# Revit family: IEK_Розетка_ОУ_C_ЗК_16А_4_мест_IP54_ГЕРМЕС_PLUS
name_source: partatom
category: Электрические приборы
units: mm (PartAtom-declared; Revit-internal decimal feet)

## family parameters
Всегда вертикально = Да
На основе рабочей плоскости = Нет
Общий = Нет
При загрузке вырезать с полостями = Нет
Размер круглого соединителя = Использовать диаметр
Сохранять ориентацию аннотаций = Да
Тип детали = Нормальный
Точка расчета площади = Нет

## types (2) — shared parameters
ADSK_URL страницы изделия = https://qr.iek.group
ADSK_Версия Revit = v2019
ADSK_Версия семейства = 01.10.25
ADSK_Группирование = Электроустановочные изделия низковольтные
ADSK_Единица измерения = шт.
ADSK_Завод-изготовитель = IEK
ADSK_Количество фаз = 1
ADSK_Количество фаз числовое = 1
ADSK_Марка = ГЕРМЕС PLUS
ADSK_Масса = 0.513
ADSK_Материал = Цвет белый
ADSK_Материал наименование = Пластик
ADSK_Напряжение = 220 В
URL = https://www.iek.ru
Высота = 72 мм
Глубина = 52 мм
Изготовитель = IEK
Описание = Изделия серии "ГЕРМЕС PLUS" используются в помещениях с повышенной влажностью или запыленностью, а также под навесом на открытом воздухе.
Степень защиты = IP54
Тип монтажа = Поверхность монтажа (открытая установка)
Ширина = 290 мм

## per-type parameters (varying)
| type | ADSK_Код изделия | ADSK_Наименование | Материал крышки |
| РСб24-3-ГПБб | ERMP32-K01-16-54-EC | Розетка 4-местная для открытой установки РСб24-3-ГПБб с заземляющим контактом IP54 ГЕРМЕС PLUS белый IEK | Цвет белый |
| РСб24-3-ГПБд | ERMP32-K03-16-54-EC | Розетка 4-местная для открытой установки РСб24-3-ГПБд с заземляющим контактом IP54 ГЕРМЕС PLUS (цвет крышки: дымчатый) IEK | Цвет дымчатый |

note: column(s) folded — value = type name in every type: ADSK_Наименование краткое
